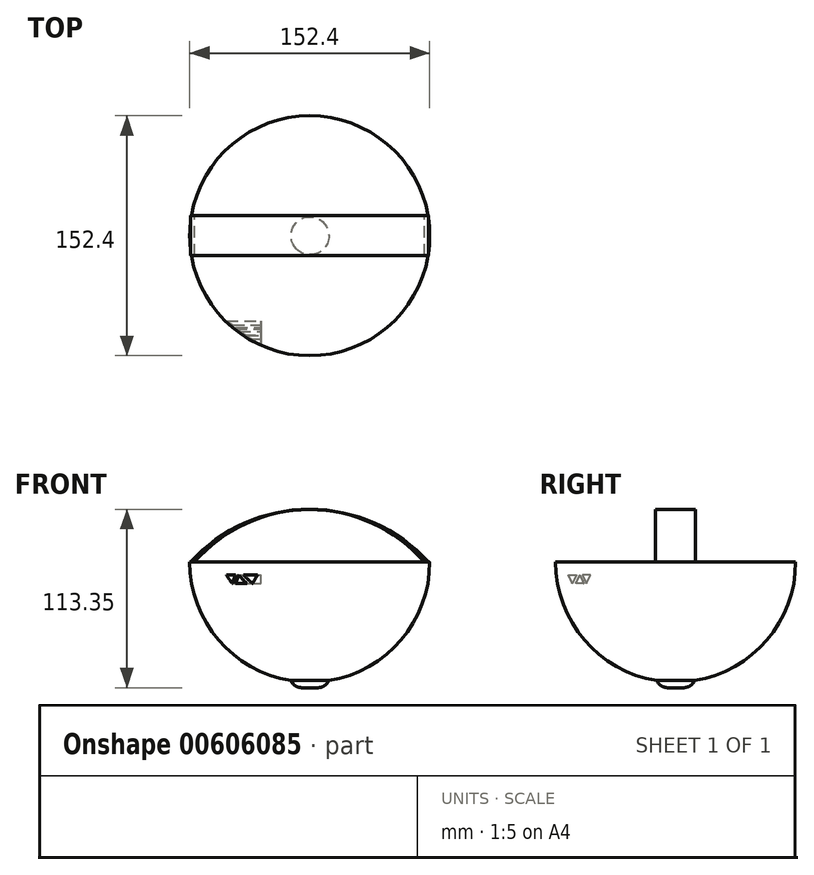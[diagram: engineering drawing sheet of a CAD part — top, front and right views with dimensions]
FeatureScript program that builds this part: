
annotation { "Feature Type Name" : "Feature", "Feature Type Description" : "" }
export const myFeature = defineFeature(function(context is Context, id is Id, definition is map)
    precondition{}
    {
        {
            var Q0;
            Q0=qCreatedBy(makeId("Front.planeOp"),FACE);
            var sketch = newSketch(context, id + "F0", { "sketchPlane" : qUnion([Q0])});
            skArc(sketch, "E0", {"start": v(76.1, 0) * mm, "mid": v(-0.1, 76.2) * mm, "end": v(-76.3, 0) * mm});
            skLineSegment(sketch, "E1", {"start": v(-76.3, 0) * mm, "end": v(76.1, 0) * mm});
            skSolve(sketch);
        }
        {
            var Q0;
            Q0 = qSketchRegion(id + "F0", true);
            var Q1;
            Q1=sQuery(id+"F0.wireOp",EDGE,"E1");
            revolve(context, id + "F1", {"entities" : qUnion([Q0]), "axis" : qUnion([Q1]), "revolveType" : RevolveType.TWO_DIRECTIONS, "oppositeDirection" : true, "angle" : 270 * degree, "angleBack" : 90 * degree});
        }
        {
            var Q0;
            Q0=qCreatedBy(makeId("Front.planeOp"),FACE);
            var sketch = newSketch(context, id + "F2", { "sketchPlane" : qUnion([Q0])});
            skArc(sketch, "E2", {"start": v(75.19, 0) * mm, "mid": v(-0.3, 33.6) * mm, "end": v(-75.78, 0) * mm});
            skArc(sketch, "E3", {"start": v(72.65, 0) * mm, "mid": v(-0.3, 33.3) * mm, "end": v(-73.24, 0) * mm});
            skLineSegment(sketch, "E4", {"start": v(-75.78, 0) * mm, "end": v(-73.24, 0) * mm});
            skLineSegment(sketch, "E5", {"start": v(75.19, 0) * mm, "end": v(72.65, 0) * mm});
            skSolve(sketch);
        }
        {
            var Q0;
            Q0 = qSketchRegion(id + "F2", true);
            extrude(context, id + "F3", {"entities" : qUnion([Q0]), "operationType" : NewBodyOperationType.ADD, "depth" : 12.7 * mm, "offsetDistance" : 25.4 * mm, "hasSecondDirection" : true, "secondDirectionOppositeDirection" : true, "secondDirectionDepth" : 12.7 * mm});
        }
        {
            var Q0;
            Q0=qCreatedBy(makeId("Right.planeOp"),FACE);
            var sketch = newSketch(context, id + "F4", { "sketchPlane" : qUnion([Q0])});
            skLineSegment(sketch, "E6", {"start": v(-54.13, -8.2) * mm, "end": v(-59.21, -8.2) * mm});
            skLineSegment(sketch, "E7", {"start": v(-59.21, -8.2) * mm, "end": v(-56.67, -13.63) * mm});
            skLineSegment(sketch, "E8", {"start": v(-56.67, -13.63) * mm, "end": v(-54.13, -8.2) * mm});
            skLineSegment(sketch, "E9", {"start": v(-60.95, -8.2) * mm, "end": v(-58.4, -13.63) * mm});
            skLineSegment(sketch, "E10", {"start": v(-58.4, -13.63) * mm, "end": v(-63.49, -13.63) * mm});
            skLineSegment(sketch, "E11", {"start": v(-63.49, -13.63) * mm, "end": v(-60.95, -8.2) * mm});
            skLineSegment(sketch, "E12", {"start": v(-63.09, -8.2) * mm, "end": v(-65.63, -13.63) * mm});
            skLineSegment(sketch, "E13", {"start": v(-65.63, -13.63) * mm, "end": v(-68.17, -8.2) * mm});
            skLineSegment(sketch, "E14", {"start": v(-68.17, -8.2) * mm, "end": v(-63.09, -8.2) * mm});
            skSolve(sketch);
        }
        {
            var Q0;
            Q0 = qSketchRegion(id + "F4", true);
            extrude(context, id + "F5", {"entities" : qUnion([Q0]), "operationType" : NewBodyOperationType.REMOVE, "oppositeDirection" : true, "depth" : 70.87 * mm, "offsetDistance" : 25.4 * mm, "hasSecondDirection" : true, "secondDirectionOppositeDirection" : true, "secondDirectionDepth" : 30.99 * mm});
        }
        {
            var Q0;
            Q0=qCreatedBy(makeId("Top.planeOp"),FACE);
            var sketch = newSketch(context, id + "F6", { "sketchPlane" : qUnion([Q0])});
            skCircle(sketch, "E15", {"center": v(0, 0) * mm, "radius": 12.03 * mm});
            skSolve(sketch);
        }
        {
            var Q0;
            Q0 = qSketchRegion(id + "F6", true);
            extrude(context, id + "F7", {"entities" : qUnion([Q0]), "operationType" : NewBodyOperationType.ADD, "oppositeDirection" : true, "depth" : 79.76 * mm, "offsetDistance" : 25.4 * mm});
        }
        {
            var Q0;
            Q0=makeQuery(id+"F7.opExtrude","CAP_EDGE",EDGE,{"disambiguationData":[OSD([sQuery(id+"F6.wireOp",EDGE,"E15")])],"isStart":false});
            fillet(context, id + "F8", {"entities" : qUnion([Q0]), "radius" : 7.62 * mm, "tangentPropagation" : true, "allowEdgeOverflow" : false});
        }
    });
